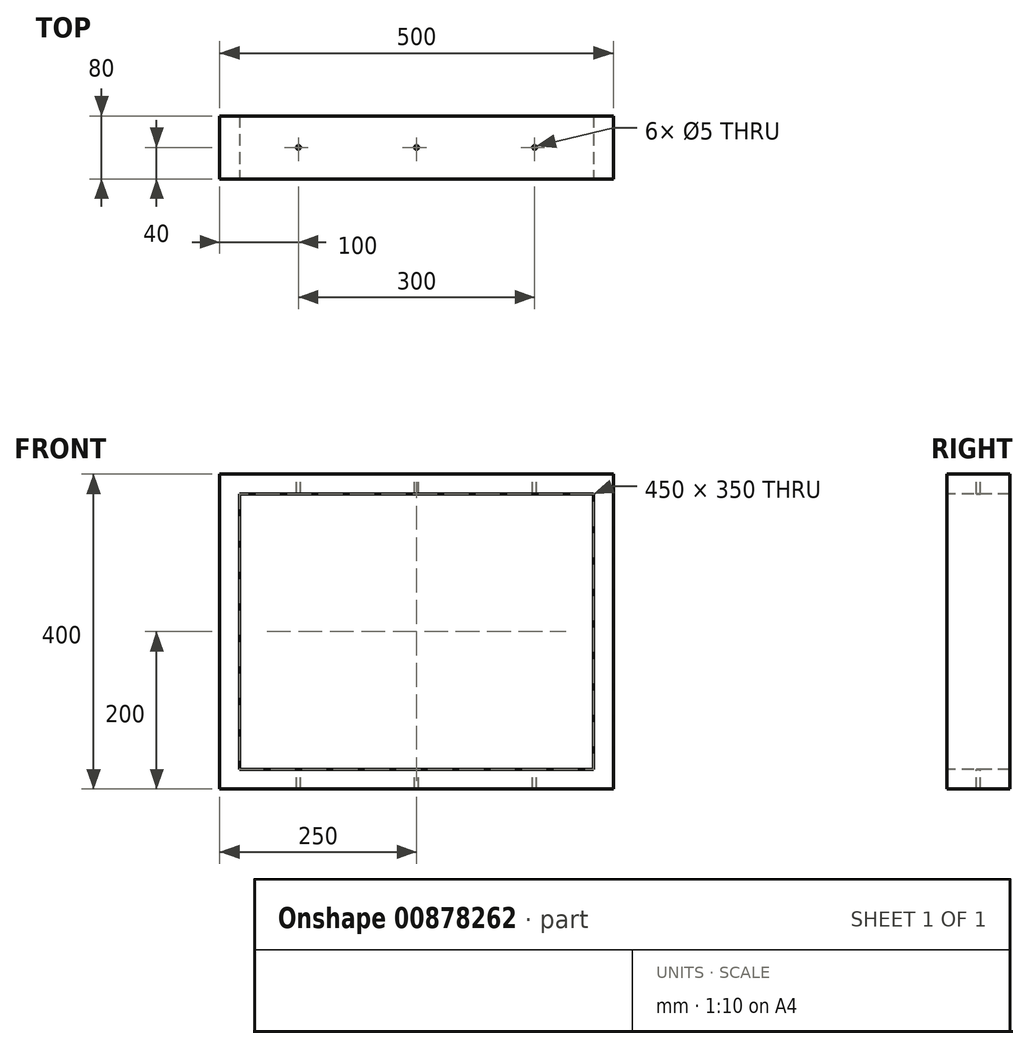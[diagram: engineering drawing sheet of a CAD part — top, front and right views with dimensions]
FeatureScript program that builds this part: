
annotation { "Feature Type Name" : "Feature", "Feature Type Description" : "" }
export const myFeature = defineFeature(function(context is Context, id is Id, definition is map)
    precondition{}
    {
        {
            var Q0;
            Q0=qCreatedBy(makeId("Front.planeOp"),FACE);
            var sketch = newSketch(context, id + "F0", { "sketchPlane" : qUnion([Q0])});
            skLineSegment(sketch, "E0.bottom", {"start": v(250, 200) * mm, "end": v(-250, 200) * mm});
            skLineSegment(sketch, "E0.top", {"start": v(250, -200) * mm, "end": v(-250, -200) * mm});
            skLineSegment(sketch, "E0.left", {"start": v(250, 200) * mm, "end": v(250, -200) * mm});
            skLineSegment(sketch, "E0.right", {"start": v(-250, 200) * mm, "end": v(-250, -200) * mm});
            skPoint(sketch, "E0.middle", {"position": v(0, 0) * mm});
            skSolve(sketch);
        }
        {
            var Q0;
            Q0 = qSketchRegion(id + "F0", true);
            extrude(context, id + "F1", {"entities" : qUnion([Q0]), "depth" : 80 * mm, "offsetDistance" : 25 * mm});
        }
        {
            var Q0;
            Q0=makeQuery(id+"F1.opExtrude","CAP_FACE",FACE,{"disambiguationData":[OSD([sQuery(id+"F0.wireOp",EDGE,"E0.bottom"),sQuery(id+"F0.wireOp",EDGE,"E0.top"),sQuery(id+"F0.wireOp",EDGE,"E0.left"),sQuery(id+"F0.wireOp",EDGE,"E0.right")])],"isStart":false});
            var sketch = newSketch(context, id + "F2", { "sketchPlane" : qUnion([Q0])});
            skLineSegment(sketch, "E1.bottom", {"start": v(225, 175) * mm, "end": v(-225, 175) * mm});
            skLineSegment(sketch, "E1.top", {"start": v(225, -175) * mm, "end": v(-225, -175) * mm});
            skLineSegment(sketch, "E1.left", {"start": v(225, 175) * mm, "end": v(225, -175) * mm});
            skLineSegment(sketch, "E1.right", {"start": v(-225, 175) * mm, "end": v(-225, -175) * mm});
            skPoint(sketch, "E1.middle", {"position": v(0, 0) * mm});
            skSolve(sketch);
        }
        {
            var Q0;
            Q0 = qSketchRegion(id + "F2", true);
            extrude(context, id + "F3", {"entities" : qUnion([Q0]), "operationType" : NewBodyOperationType.REMOVE, "endBound" : BoundingType.UP_TO_NEXT, "oppositeDirection" : true, "depth" : 25 * mm, "offsetDistance" : 25 * mm});
        }
        {
            var Q0;
            Q0=makeQuery(id+"F1.opExtrude","SWEPT_FACE",FACE,{"disambiguationData":[OSD([sQuery(id+"F0.wireOp",EDGE,"E0.bottom")])]});
            var sketch = newSketch(context, id + "F4", { "sketchPlane" : qUnion([Q0])});
            skCircle(sketch, "E2", {"center": v(-150, -40) * mm, "radius": 2.5 * mm});
            skPoint(sketch, "E2.centerSnap0", {"position": v(-250, -40) * mm});
            skCircle(sketch, "E3", {"center": v(0, -40) * mm, "radius": 2.5 * mm});
            skCircle(sketch, "E4", {"center": v(150, -40) * mm, "radius": 2.5 * mm});
            skSolve(sketch);
        }
        {
            var Q0;
            Q0 = qSketchRegion(id + "F4", true);
            extrude(context, id + "F5", {"entities" : qUnion([Q0]), "operationType" : NewBodyOperationType.REMOVE, "endBound" : BoundingType.THROUGH_ALL, "oppositeDirection" : true, "depth" : 25 * mm, "offsetDistance" : 25 * mm});
        }
    });
